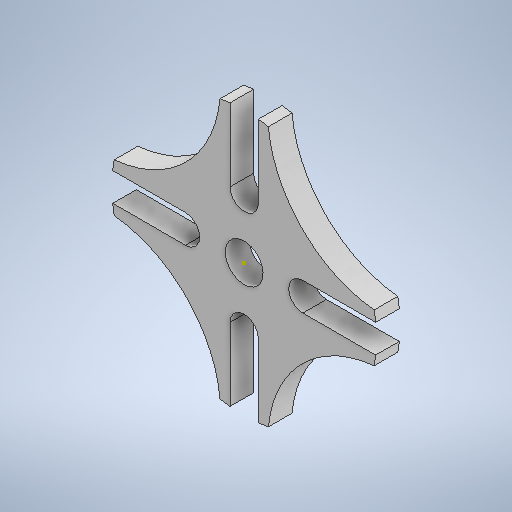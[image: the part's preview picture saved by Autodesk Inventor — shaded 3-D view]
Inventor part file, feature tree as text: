
AUTODESK INVENTOR PART (.ipt)
format: ipt  version: 2025.2 (Build 292293000, 293)  size: 277,504 bytes
history: native  units: mm
features: sketch x4, extrude x2, pattern_circular x1
ambient origin geometry x8: Origin, YZ Plane, XZ Plane, XY Plane, X Axis, Y Axis, Z Axis, Center Point
bodies: Solid1 (feature_tree)
feature tree (7):
  extrude  "Extrusion1"  Depth=5.0mm TaperAngle=0.0deg
  sketch  "Sketch2"  dims[d3=30.0mm d4=30.0mm d5=60.0mm]
  sketch  "Sketch3"  dims[d6=60.0mm]
  sketch  "Sketch4"  dims[d7=50.0mm d8=8.0mm d9=6.0mm d10=5.0mm d11=0.0mm d12=40.0mm d13=360.0deg]
  extrude  "Extrusion2"  Depth=30.0mm
  pattern_circular  "Circular Pattern1"  Count=6  [1 undecoded]
  sketch  "Sketch1"  dims[d0=56.0mm d1=5.0mm d2=0.0mm]
note: 1 required parameter value undecoded (feature->parameter linkage not recoverable at this tier; creation-order binding heuristic only, values carry confidence <= 0.55)
